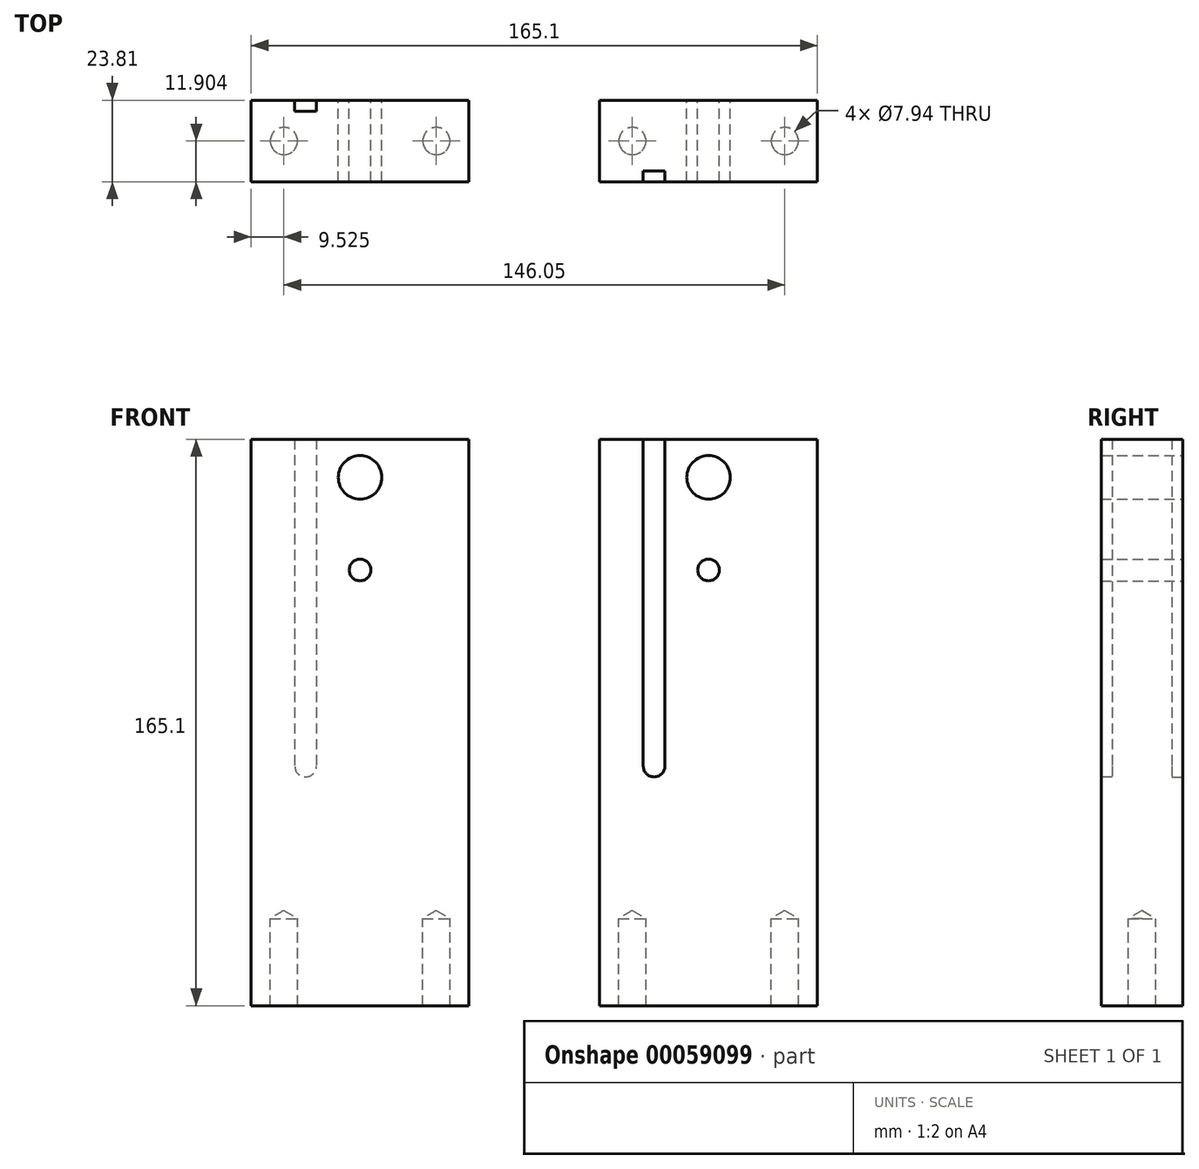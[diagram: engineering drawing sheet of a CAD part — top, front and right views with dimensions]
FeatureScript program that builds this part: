
annotation { "Feature Type Name" : "Feature", "Feature Type Description" : "" }
export const myFeature = defineFeature(function(context is Context, id is Id, definition is map)
    precondition{}
    {
        {
            var Q0;
            Q0=qCreatedBy(makeId("Front.planeOp"),FACE);
            var sketch = newSketch(context, id + "F0", { "sketchPlane" : qUnion([Q0])});
            skLineSegment(sketch, "E0.rect.bottom", {"start": v(31.75, -82.55) * mm, "end": v(-31.75, -82.55) * mm});
            skLineSegment(sketch, "E0.rect.top", {"start": v(31.75, 82.55) * mm, "end": v(-31.75, 82.55) * mm});
            skLineSegment(sketch, "E0.rect.left", {"start": v(31.75, -82.55) * mm, "end": v(31.75, 82.55) * mm});
            skLineSegment(sketch, "E0.rect.right", {"start": v(-31.75, -82.55) * mm, "end": v(-31.75, 82.55) * mm});
            skPoint(sketch, "E0.rect.middle", {"position": v(0, 0) * mm});
            skLineSegment(sketch, "E1", {"start": v(0, 82.55) * mm, "end": v(0, -82.55) * mm, "construction": true});
            skLineSegment(sketch, "E2", {"start": v(-31.75, 71.42) * mm, "end": v(31.75, 71.42) * mm, "construction": true});
            skLineSegment(sketch, "E3", {"start": v(-31.75, 44.45) * mm, "end": v(31.75, 44.45) * mm, "construction": true});
            skCircle(sketch, "E4", {"center": v(0, 71.42) * mm, "radius": 6.35 * mm});
            skCircle(sketch, "E5", {"center": v(0, 44.45) * mm, "radius": 3.18 * mm});
            skSolve(sketch);
        }
        {
            var Q0;
            Q0=makeQuery(id+"F0.imprint","IMPRINT",FACE,{"disambiguationData":[TD([[makeQuery(id+"F0.imprint","IMPRINT",EDGE,{"derivedFrom":sQuery(id+"F0.wireOp",EDGE,"E0.rect.bottom")}),-1.0]])]});
            extrude(context, id + "F1", {"entities" : qUnion([Q0]), "depth" : 23.8 * mm});
        }
        {
            var Q0;
            Q0=makeQuery(id+"F1.opExtrude","SWEPT_FACE",FACE,{"disambiguationData":[OSD([sQuery(id+"F0.wireOp",EDGE,"E0.rect.bottom")])]});
            var sketch = newSketch(context, id + "F2", { "sketchPlane" : qUnion([Q0])});
            skLineSegment(sketch, "E6", {"start": v(-31.75, 11.9) * mm, "end": v(31.75, 11.9) * mm, "construction": true});
            skLineSegment(sketch, "E7", {"start": v(-22.23, 23.81) * mm, "end": v(-22.23, 0) * mm, "construction": true});
            skLineSegment(sketch, "E8", {"start": v(22.22, 23.81) * mm, "end": v(22.22, 0) * mm, "construction": true});
            skPoint(sketch, "E9", {"position": v(-22.23, 11.9) * mm});
            skPoint(sketch, "E10", {"position": v(22.22, 11.9) * mm});
            skSolve(sketch);
        }
        {
            var Q0;
            Q0=sQuery(id+"F2.wireOp",VERTEX,"E9");
            var Q1;
            Q1=sQuery(id+"F2.wireOp",VERTEX,"E10");
            var Q2;
            Q2=makeQuery(id+"F1.opExtrude","SWEPT_BODY",BODY,{"disambiguationData":[OSD([sQuery(id+"F0.wireOp",EDGE,"E0.rect.bottom"),sQuery(id+"F0.wireOp",EDGE,"E0.rect.top"),sQuery(id+"F0.wireOp",EDGE,"E0.rect.left"),sQuery(id+"F0.wireOp",EDGE,"E0.rect.right"),sQuery(id+"F0.wireOp",EDGE,"E4"),sQuery(id+"F0.wireOp",EDGE,"E5")])]});
            hole(context, id + "F3", {"style" : HoleStyle.SIMPLE, "endStyle" : HoleEndStyle.BLIND, "standardTappedOrClearance" : lookupTablePath({ "standard" : "ANSI", "engagement" : "75%", "pitch" : "16 tpi", "size" : "3/8", "type" : "Tapped" }), "standardBlindInLast" : lookupTablePath({ "standard" : "ANSI", "engagement" : "75%", "pitch" : "16 tpi", "size" : "3/8", "type" : "Tapped" }), "holeDiameter" : 7.94 * mm, "holeDepth" : 25.4 * mm, "locations" : qUnion([Q0, Q1]), "scope" : qUnion([Q2]), "majorDiameter" : 9.53 * mm});
        }
        {
            var Q0;
            Q0=makeQuery(id+"F1.opExtrude","SWEPT_BODY",BODY,{"disambiguationData":[OSD([sQuery(id+"F0.wireOp",EDGE,"E0.rect.bottom"),sQuery(id+"F0.wireOp",EDGE,"E0.rect.top"),sQuery(id+"F0.wireOp",EDGE,"E0.rect.left"),sQuery(id+"F0.wireOp",EDGE,"E0.rect.right"),sQuery(id+"F0.wireOp",EDGE,"E4"),sQuery(id+"F0.wireOp",EDGE,"E5")])]});
            var Q1;
            Q1=makeQuery(id+"F1.opExtrude","CAP_EDGE",EDGE,{"disambiguationData":[OSD([sQuery(id+"F0.wireOp",EDGE,"E0.rect.top")])],"isStart":false});
            transform(context, id + "F4", {"entities" : qUnion([Q0]), "transformType" : TransformType.TRANSLATION_DISTANCE, "transformDirection" : qUnion([Q1]), "distance" : 101.6 * mm, "makeCopy" : true});
        }
        {
            var Q0;
            Q0=makeQuery(id+"F1.opExtrude","CAP_FACE",FACE,{"disambiguationData":[OSD([sQuery(id+"F0.wireOp",EDGE,"E0.rect.bottom"),sQuery(id+"F0.wireOp",EDGE,"E0.rect.top"),sQuery(id+"F0.wireOp",EDGE,"E0.rect.left"),sQuery(id+"F0.wireOp",EDGE,"E0.rect.right"),sQuery(id+"F0.wireOp",EDGE,"E4"),sQuery(id+"F0.wireOp",EDGE,"E5")])],"isStart":false});
            var sketch = newSketch(context, id + "F5", { "sketchPlane" : qUnion([Q0])});
            skLineSegment(sketch, "E11", {"start": v(-19.05, 82.55) * mm, "end": v(-19.05, -12.7) * mm});
            skLineSegment(sketch, "E12", {"start": v(-12.7, 82.55) * mm, "end": v(-12.7, -12.7) * mm});
            skArc(sketch, "E13", {"start": v(-19.05, -12.7) * mm, "mid": v(-15.88, -15.88) * mm, "end": v(-12.7, -12.7) * mm});
            skSolve(sketch);
        }
        {
            var Q0;
            {var subQ0=sQuery(id+"F5.wireOp",EDGE,"E11");Q0=makeQuery(id+"F5.imprint","IMPRINT",FACE,{"disambiguationData":[TD([[makeQuery(id+"F5.imprint","IMPRINT",EDGE,{"derivedFrom":subQ0}),1.0]])]});}
            extrude(context, id + "F6", {"entities" : qUnion([Q0]), "operationType" : NewBodyOperationType.REMOVE, "oppositeDirection" : true, "depth" : 3.17 * mm});
        }
        {
            var Q0;
            Q0=makeQuery(id+"F4.opPattern","COPY",FACE,{"derivedFrom":makeQuery(id+"F1.opExtrude","CAP_FACE",FACE,{"disambiguationData":[OSD([sQuery(id+"F0.wireOp",EDGE,"E0.rect.bottom"),sQuery(id+"F0.wireOp",EDGE,"E0.rect.top"),sQuery(id+"F0.wireOp",EDGE,"E0.rect.left"),sQuery(id+"F0.wireOp",EDGE,"E0.rect.right"),sQuery(id+"F0.wireOp",EDGE,"E4"),sQuery(id+"F0.wireOp",EDGE,"E5")])],"isStart":true}),"instanceName":"1"});
            var sketch = newSketch(context, id + "F7", { "sketchPlane" : qUnion([Q0])});
            skLineSegment(sketch, "E14", {"start": v(114.3, 82.55) * mm, "end": v(114.3, -12.7) * mm});
            skLineSegment(sketch, "E15", {"start": v(120.65, 82.55) * mm, "end": v(120.65, -12.7) * mm});
            skArc(sketch, "E16", {"start": v(114.3, -12.7) * mm, "mid": v(117.48, -15.88) * mm, "end": v(120.65, -12.7) * mm});
            skSolve(sketch);
        }
        {
            var Q0;
            {var subQ0=sQuery(id+"F7.wireOp",EDGE,"E14");Q0=makeQuery(id+"F7.imprint","IMPRINT",FACE,{"disambiguationData":[TD([[makeQuery(id+"F7.imprint","IMPRINT",EDGE,{"derivedFrom":subQ0}),1.0]])]});}
            extrude(context, id + "F8", {"entities" : qUnion([Q0]), "operationType" : NewBodyOperationType.REMOVE, "oppositeDirection" : true, "depth" : 3.17 * mm});
        }
    });
